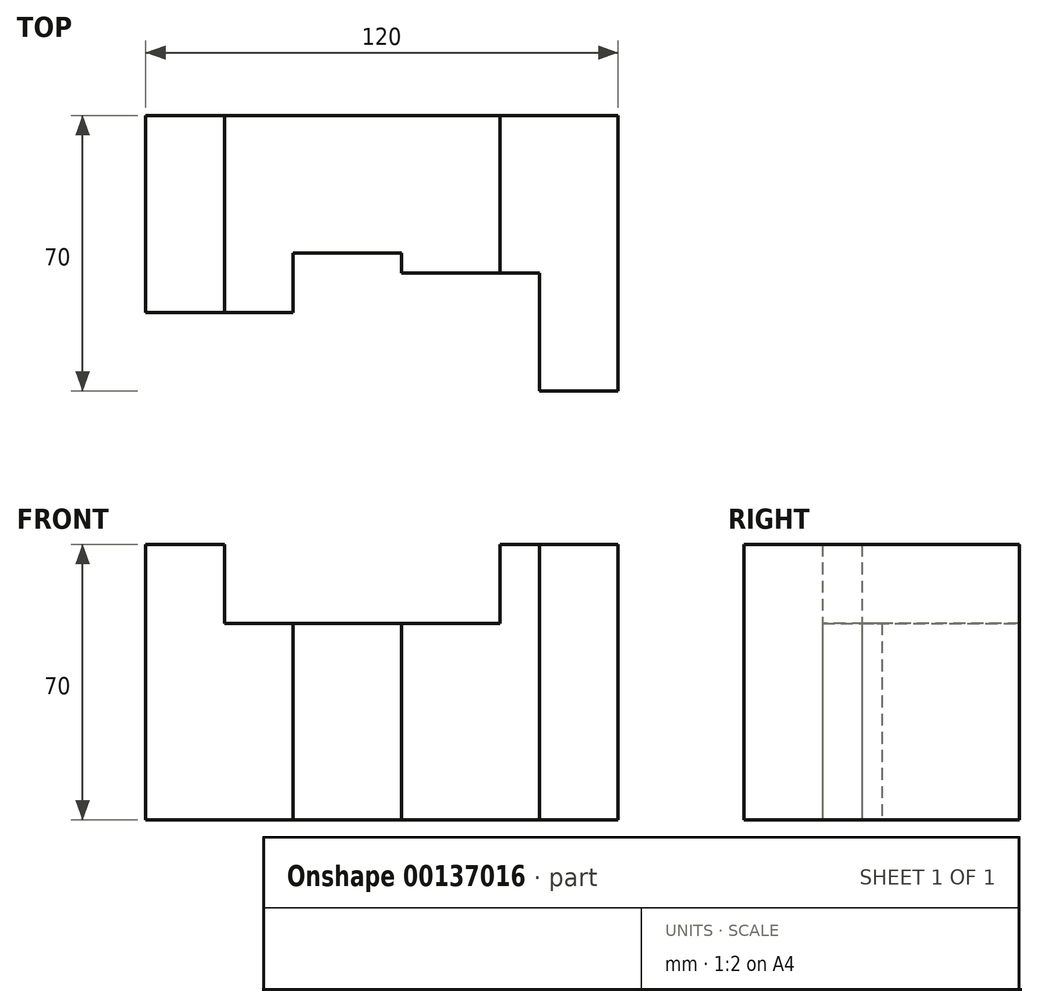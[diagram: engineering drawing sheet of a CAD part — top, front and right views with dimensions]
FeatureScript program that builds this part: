
annotation { "Feature Type Name" : "Feature", "Feature Type Description" : "" }
export const myFeature = defineFeature(function(context is Context, id is Id, definition is map)
    precondition{}
    {
        {
            var Q0;
            Q0=qCreatedBy(makeId("Top.planeOp"),FACE);
            var sketch = newSketch(context, id + "F0", { "sketchPlane" : qUnion([Q0])});
            skLineSegment(sketch, "E0", {"start": v(-35, 35) * mm, "end": v(35, 35) * mm});
            skLineSegment(sketch, "E1", {"start": v(35, 35) * mm, "end": v(35, -5) * mm});
            skLineSegment(sketch, "E2", {"start": v(35, -5) * mm, "end": v(10, -5) * mm});
            skLineSegment(sketch, "E3", {"start": v(10, -5) * mm, "end": v(10, 0) * mm});
            skLineSegment(sketch, "E4", {"start": v(10, 0) * mm, "end": v(-17.5, 0) * mm});
            skLineSegment(sketch, "E5", {"start": v(-17.5, 0) * mm, "end": v(-17.5, -15) * mm});
            skLineSegment(sketch, "E6", {"start": v(-35, -15) * mm, "end": v(-35, 35) * mm});
            skLineSegment(sketch, "E7", {"start": v(-17.5, -15) * mm, "end": v(-35, -15) * mm});
            skLineSegment(sketch, "E8", {"start": v(0, 46.8) * mm, "end": v(0, -21.57) * mm, "construction": true});
            skSolve(sketch);
        }
        {
            var Q0;
            Q0=makeQuery(id+"F0.imprint","IMPRINT",FACE,{"disambiguationData":[TD([[makeQuery(id+"F0.imprint","IMPRINT",EDGE,{"derivedFrom":sQuery(id+"F0.wireOp",EDGE,"E0")}),-1.0]])]});
            extrude(context, id + "F1", {"entities" : qUnion([Q0]), "depth" : 50 * mm});
        }
        {
            var Q0;
            Q0=makeQuery(id+"F1.opExtrude","CAP_FACE",FACE,{"disambiguationData":[OSD([sQuery(id+"F0.wireOp",EDGE,"E0"),sQuery(id+"F0.wireOp",EDGE,"E1"),sQuery(id+"F0.wireOp",EDGE,"E2"),sQuery(id+"F0.wireOp",EDGE,"E3"),sQuery(id+"F0.wireOp",EDGE,"E4"),sQuery(id+"F0.wireOp",EDGE,"E5"),sQuery(id+"F0.wireOp",EDGE,"E6"),sQuery(id+"F0.wireOp",EDGE,"E7")])],"isStart":false});
            var sketch = newSketch(context, id + "F2", { "sketchPlane" : qUnion([Q0])});
            skLineSegment(sketch, "E9", {"start": v(35, 35) * mm, "end": v(65, 35) * mm});
            skLineSegment(sketch, "E10", {"start": v(65, 35) * mm, "end": v(65, -35) * mm});
            skLineSegment(sketch, "E11", {"start": v(65, -35) * mm, "end": v(45, -35) * mm});
            skLineSegment(sketch, "E12", {"start": v(45, -35) * mm, "end": v(45, -5) * mm});
            skLineSegment(sketch, "E13", {"start": v(45, -5) * mm, "end": v(35, -5) * mm});
            skLineSegment(sketch, "E14", {"start": v(35, -5) * mm, "end": v(35, 35) * mm});
            skLineSegment(sketch, "E15", {"start": v(-35, -15) * mm, "end": v(-35, 35) * mm});
            skLineSegment(sketch, "E16", {"start": v(-35, 35) * mm, "end": v(-55, 35) * mm});
            skLineSegment(sketch, "E17", {"start": v(-55, 35) * mm, "end": v(-55, -15) * mm});
            skLineSegment(sketch, "E18", {"start": v(-55, -15) * mm, "end": v(-35, -15) * mm});
            skSolve(sketch);
        }
        {
            var Q0;
            Q0=makeQuery(id+"F2.imprint","IMPRINT",FACE,{"disambiguationData":[TD([[makeQuery(id+"F2.imprint","IMPRINT",EDGE,{"derivedFrom":sQuery(id+"F2.wireOp",EDGE,"E9")}),-1.0]])]});
            var Q1;
            Q1=makeQuery(id+"F2.imprint","IMPRINT",FACE,{"disambiguationData":[TD([[makeQuery(id+"F2.imprint","IMPRINT",EDGE,{"derivedFrom":sQuery(id+"F2.wireOp",EDGE,"E15")}),1.0]])]});
            extrude(context, id + "F3", {"entities" : qUnion([Q0, Q1]), "operationType" : NewBodyOperationType.ADD, "depth" : 20 * mm, "hasSecondDirection" : true, "secondDirectionOppositeDirection" : true, "secondDirectionDepth" : 50 * mm});
        }
    });
